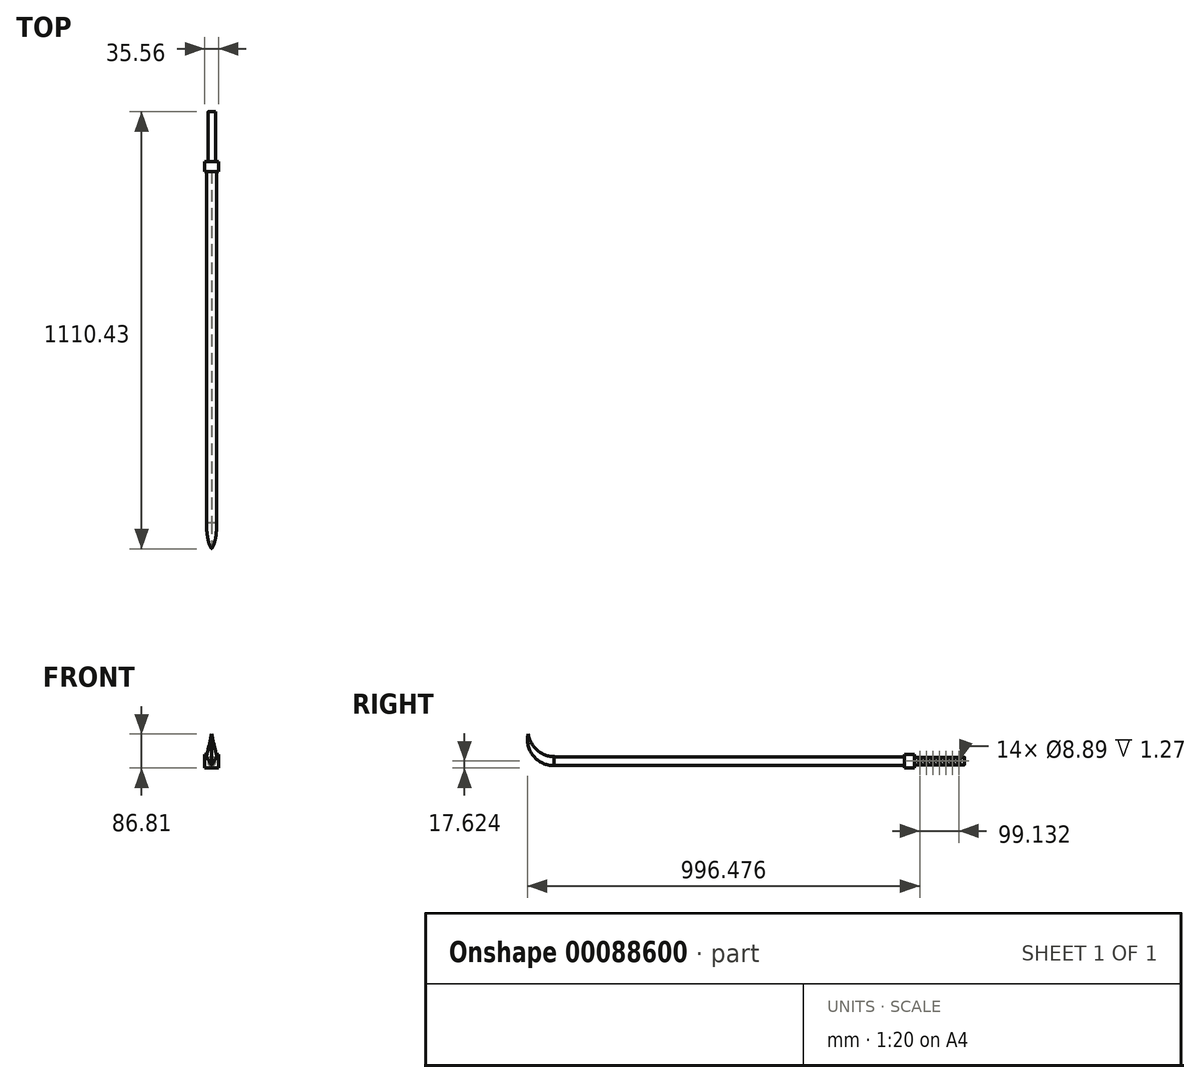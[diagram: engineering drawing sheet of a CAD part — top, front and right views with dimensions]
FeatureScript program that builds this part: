
annotation { "Feature Type Name" : "Feature", "Feature Type Description" : "" }
export const myFeature = defineFeature(function(context is Context, id is Id, definition is map)
    precondition{}
    {
        {
            var Q0;
            Q0=qCreatedBy(makeId("Right.planeOp"),FACE);
            var sketch = newSketch(context, id + "F0", { "sketchPlane" : qUnion([Q0])});
            skArc(sketch, "E0", {"start": v(-281.73, 35.1) * mm, "mid": v(-258.73, -6.34) * mm, "end": v(-214.29, -22.8) * mm});
            skArc(sketch, "E1", {"start": v(-281.73, 35.1) * mm, "mid": v(-268.38, -21.13) * mm, "end": v(-215.9, -45.35) * mm});
            skLineSegment(sketch, "E2", {"start": v(-214.29, -22.8) * mm, "end": v(674.71, -22.8) * mm});
            skLineSegment(sketch, "E3", {"start": v(-215.9, -45.35) * mm, "end": v(674.71, -45.35) * mm});
            skLineSegment(sketch, "E4", {"start": v(674.71, -22.8) * mm, "end": v(674.71, -45.35) * mm});
            skSolve(sketch);
        }
        {
            var Q0;
            Q0 = qSketchRegion(id + "F0", true);
            extrude(context, id + "F1", {"entities" : qUnion([Q0]), "depth" : 25.4 * mm});
        }
        {
            var Q0;
            Q0=makeQuery(id+"F1.opExtrude","SWEPT_FACE",FACE,{"disambiguationData":[OSD([sQuery(id+"F0.wireOp",EDGE,"E4")])]});
            var sketch = newSketch(context, id + "F2", { "sketchPlane" : qUnion([Q0])});
            skLineSegment(sketch, "E5", {"start": v(-25.4, -22.8) * mm, "end": v(-12.7, -45.35) * mm});
            skLineSegment(sketch, "E6", {"start": v(-12.7, -45.35) * mm, "end": v(0, -22.8) * mm});
            skSolve(sketch);
        }
        {
            var Q0;
            {var subQ0=sQuery(id+"F2.wireOp",EDGE,"E5");Q0=makeQuery(id+"F2.imprint","IMPRINT",FACE,{"disambiguationData":[TD([[makeQuery(id+"F2.imprint","IMPRINT",EDGE,{"derivedFrom":subQ0}),-1.0]])]});}
            var Q1;
            {var subQ0=sQuery(id+"F2.wireOp",EDGE,"E6");Q1=makeQuery(id+"F2.imprint","IMPRINT",FACE,{"disambiguationData":[TD([[makeQuery(id+"F2.imprint","IMPRINT",EDGE,{"derivedFrom":subQ0}),-1.0]])]});}
            var Q2;
            Q2=makeQuery(id+"F1.opExtrude","CAP_EDGE",EDGE,{"disambiguationData":[OSD([sQuery(id+"F0.wireOp",EDGE,"E3")])],"isStart":false});
            var Q3;
            Q3=makeQuery(id+"F1.opExtrude","CAP_EDGE",EDGE,{"disambiguationData":[OSD([sQuery(id+"F0.wireOp",EDGE,"E1")])],"isStart":false});
            sweep(context, id + "F3", {"operationType" : NewBodyOperationType.REMOVE, "profiles" : qUnion([Q0, Q1]), "path" : qUnion([Q2, Q3])});
        }
        {
            var Q0;
            Q0=makeQuery(id+"F1.opExtrude","SWEPT_FACE",FACE,{"disambiguationData":[OSD([sQuery(id+"F0.wireOp",EDGE,"E4")])]});
            var sketch = newSketch(context, id + "F4", { "sketchPlane" : qUnion([Q0])});
            skLineSegment(sketch, "E7", {"start": v(-12.7, -45.35) * mm, "end": v(-12.7, -22.8) * mm});
            skLineSegment(sketch, "E8", {"start": v(-12.7, -22.8) * mm, "end": v(-12.7, -16.45) * mm});
            skLineSegment(sketch, "E9", {"start": v(-12.7, -45.35) * mm, "end": v(-12.7, -51.7) * mm});
            skLineSegment(sketch, "E10", {"start": v(-12.7, -16.45) * mm, "end": v(-30.48, -16.45) * mm});
            skLineSegment(sketch, "E11", {"start": v(-12.7, -16.45) * mm, "end": v(5.08, -16.45) * mm});
            skLineSegment(sketch, "E12", {"start": v(-12.7, -51.7) * mm, "end": v(5.08, -51.7) * mm});
            skLineSegment(sketch, "E13", {"start": v(5.08, -51.7) * mm, "end": v(5.08, -16.45) * mm});
            skLineSegment(sketch, "E14", {"start": v(-12.7, -51.7) * mm, "end": v(-30.48, -51.7) * mm});
            skLineSegment(sketch, "E15", {"start": v(-30.48, -51.7) * mm, "end": v(-30.48, -16.45) * mm});
            skLineSegment(sketch, "E16", {"start": v(-19.05, -34.08) * mm, "end": v(-30.48, -34.08) * mm});
            skLineSegment(sketch, "E17", {"start": v(-6.35, -34.08) * mm, "end": v(5.08, -34.08) * mm});
            skSolve(sketch);
        }
        {
            var Q0;
            Q0 = qSketchRegion(id + "F4", true);
            extrude(context, id + "F5", {"entities" : qUnion([Q0]), "depth" : 25.4 * mm});
        }
        {
            var Q0;
            Q0=makeQuery(id+"F5.opExtrude","CAP_FACE",FACE,{"disambiguationData":[OSD([sQuery(id+"F4.wireOp",EDGE,"E10"),sQuery(id+"F4.wireOp",EDGE,"E11"),sQuery(id+"F4.wireOp",EDGE,"E12"),sQuery(id+"F4.wireOp",EDGE,"E13"),sQuery(id+"F4.wireOp",EDGE,"E14"),sQuery(id+"F4.wireOp",EDGE,"E15")])],"isStart":false});
            var sketch = newSketch(context, id + "F6", { "sketchPlane" : qUnion([Q0])});
            skLineSegment(sketch, "E18", {"start": v(-12.7, -34.08) * mm, "end": v(-12.7, -24.55) * mm});
            skLineSegment(sketch, "E19", {"start": v(-12.7, -34.08) * mm, "end": v(-12.7, -43.6) * mm});
            skLineSegment(sketch, "E20", {"start": v(-12.7, -34.08) * mm, "end": v(-3.18, -34.08) * mm});
            skLineSegment(sketch, "E21", {"start": v(-12.7, -34.08) * mm, "end": v(-22.22, -34.08) * mm});
            skLineSegment(sketch, "E22", {"start": v(-22.22, -34.08) * mm, "end": v(-22.22, -24.55) * mm});
            skLineSegment(sketch, "E23", {"start": v(-22.22, -24.55) * mm, "end": v(-3.18, -24.55) * mm});
            skLineSegment(sketch, "E24", {"start": v(-3.18, -24.55) * mm, "end": v(-3.18, -43.6) * mm});
            skLineSegment(sketch, "E25", {"start": v(-3.18, -43.6) * mm, "end": v(-22.22, -43.6) * mm});
            skLineSegment(sketch, "E26", {"start": v(-22.22, -43.6) * mm, "end": v(-22.22, -34.08) * mm});
            skSolve(sketch);
        }
        {
            var Q0;
            Q0 = qSketchRegion(id + "F6", true);
            extrude(context, id + "F7", {"entities" : qUnion([Q0]), "operationType" : NewBodyOperationType.ADD, "depth" : 127 * mm});
        }
        {
            var Q0;
            Q0=makeQuery(id+"F7.opExtrude","SWEPT_EDGE",EDGE,{"disambiguationData":[OSD([sQuery(id+"F6.wireOp",EDGE,"E22"),sQuery(id+"F6.wireOp",EDGE,"E23")])]});
            var Q1;
            Q1=makeQuery(id+"F7.opExtrude","SWEPT_EDGE",EDGE,{"disambiguationData":[OSD([sQuery(id+"F6.wireOp",EDGE,"E23"),sQuery(id+"F6.wireOp",EDGE,"E24")])]});
            var Q2;
            Q2=makeQuery(id+"F7.opExtrude","SWEPT_EDGE",EDGE,{"disambiguationData":[OSD([sQuery(id+"F6.wireOp",EDGE,"E25"),sQuery(id+"F6.wireOp",EDGE,"E26")])]});
            var Q3;
            Q3=makeQuery(id+"F7.opExtrude","SWEPT_EDGE",EDGE,{"disambiguationData":[OSD([sQuery(id+"F6.wireOp",EDGE,"E24"),sQuery(id+"F6.wireOp",EDGE,"E25")])]});
            fillet(context, id + "F8", {"entities" : qUnion([Q0, Q1, Q2, Q3]), "radius" : 5.08 * mm, "tangentPropagation" : true, "allowEdgeOverflow" : false});
        }
        {
            var Q0;
            Q0=makeQuery(id+"F7.opExtrude","SWEPT_FACE",FACE,{"disambiguationData":[OSD([sQuery(id+"F6.wireOp",EDGE,"E24")])]});
            var sketch = newSketch(context, id + "F9", { "sketchPlane" : qUnion([Q0])});
            skLineSegment(sketch, "E27", {"start": v(-812.22, -29.63) * mm, "end": v(-812.22, -38.52) * mm});
            skCircle(sketch, "E28", {"center": v(-812.22, -34.08) * mm, "radius": 4.44 * mm});
            skCircle(sketch, "E29.1.0.0", {"center": v(-795.7, -34.08) * mm, "radius": 4.44 * mm});
            skCircle(sketch, "E29.2.0.0", {"center": v(-779.2, -34.08) * mm, "radius": 4.44 * mm});
            skCircle(sketch, "E29.3.0.0", {"center": v(-762.69, -34.08) * mm, "radius": 4.44 * mm});
            skCircle(sketch, "E29.4.0.0", {"center": v(-746.18, -34.08) * mm, "radius": 4.44 * mm});
            skCircle(sketch, "E29.5.0.0", {"center": v(-729.67, -34.08) * mm, "radius": 4.44 * mm});
            skCircle(sketch, "E29.6.0.0", {"center": v(-713.16, -34.08) * mm, "radius": 4.44 * mm});
            skLineSegment(sketch, "E29.direction1", {"start": v(-812.22, -34.08) * mm, "end": v(-795.7, -34.08) * mm, "construction": true});
            skSolve(sketch);
        }
        {
            var Q0;
            Q0=makeQuery(id+"F7.opExtrude","SWEPT_FACE",FACE,{"disambiguationData":[OSD([sQuery(id+"F6.wireOp",EDGE,"E22"),sQuery(id+"F6.wireOp",EDGE,"E26")])]});
            var sketch = newSketch(context, id + "F10", { "sketchPlane" : qUnion([Q0])});
            skLineSegment(sketch, "E30", {"start": v(812.29, -29.63) * mm, "end": v(812.29, -38.52) * mm});
            skCircle(sketch, "E31", {"center": v(812.29, -34.08) * mm, "radius": 4.44 * mm});
            skCircle(sketch, "E32.1.0.0", {"center": v(795.78, -34.08) * mm, "radius": 4.44 * mm});
            skCircle(sketch, "E32.2.0.0", {"center": v(779.27, -34.08) * mm, "radius": 4.44 * mm});
            skCircle(sketch, "E32.3.0.0", {"center": v(762.76, -34.08) * mm, "radius": 4.44 * mm});
            skCircle(sketch, "E32.4.0.0", {"center": v(746.25, -34.08) * mm, "radius": 4.44 * mm});
            skCircle(sketch, "E32.5.0.0", {"center": v(729.74, -34.08) * mm, "radius": 4.44 * mm});
            skCircle(sketch, "E32.6.0.0", {"center": v(713.23, -34.08) * mm, "radius": 4.44 * mm});
            skLineSegment(sketch, "E32.direction1", {"start": v(812.29, -34.08) * mm, "end": v(795.78, -34.08) * mm, "construction": true});
            skSolve(sketch);
        }
        {
            var Q0;
            {var subQ0=sQuery(id+"F10.wireOp",EDGE,"E32.6.0.0");var subQ1=sQuery(id+"F6.wireOp",EDGE,"E26");var subQ2=sQuery(id+"F6.wireOp",EDGE,"E22");var subQ3=makeQuery(id+"F7.opExtrude","SWEPT_FACE",FACE,{"disambiguationData":[OSD([subQ2,subQ1])]});var subQ4=makeQuery(id+"F10.imprint","INTERSECT",VERTEX,{"derivedFrom":[makeQuery(id+"F8.opFillet","BLEND_EDGE",EDGE,{"blendedFrom":[makeQuery(id+"F7.opExtrude","SWEPT_EDGE",EDGE,{"disambiguationData":[OSD([subQ2,sQuery(id+"F6.wireOp",EDGE,"E23")])]}),subQ3],"blendedInto":[subQ3]}),subQ0]});Q0=makeQuery(id+"F10.imprint","IMPRINT",FACE,{"disambiguationData":[TD([[makeQuery(id+"F10.imprint","IMPRINT",EDGE,{"disambiguationData":[TD([[subQ4,-1.0]])],"derivedFrom":subQ0}),1.0]])]});}
            var Q1;
            {var subQ0=sQuery(id+"F10.wireOp",EDGE,"E32.5.0.0");var subQ1=sQuery(id+"F6.wireOp",EDGE,"E26");var subQ2=sQuery(id+"F6.wireOp",EDGE,"E22");var subQ3=makeQuery(id+"F7.opExtrude","SWEPT_FACE",FACE,{"disambiguationData":[OSD([subQ2,subQ1])]});var subQ4=makeQuery(id+"F10.imprint","INTERSECT",VERTEX,{"derivedFrom":[makeQuery(id+"F8.opFillet","BLEND_EDGE",EDGE,{"blendedFrom":[makeQuery(id+"F7.opExtrude","SWEPT_EDGE",EDGE,{"disambiguationData":[OSD([subQ2,sQuery(id+"F6.wireOp",EDGE,"E23")])]}),subQ3],"blendedInto":[subQ3]}),subQ0]});Q1=makeQuery(id+"F10.imprint","IMPRINT",FACE,{"disambiguationData":[TD([[makeQuery(id+"F10.imprint","IMPRINT",EDGE,{"disambiguationData":[TD([[subQ4,-1.0]])],"derivedFrom":subQ0}),1.0]])]});}
            var Q2;
            {var subQ0=sQuery(id+"F10.wireOp",EDGE,"E32.4.0.0");var subQ1=sQuery(id+"F6.wireOp",EDGE,"E26");var subQ2=sQuery(id+"F6.wireOp",EDGE,"E22");var subQ3=makeQuery(id+"F7.opExtrude","SWEPT_FACE",FACE,{"disambiguationData":[OSD([subQ2,subQ1])]});var subQ4=makeQuery(id+"F10.imprint","INTERSECT",VERTEX,{"derivedFrom":[makeQuery(id+"F8.opFillet","BLEND_EDGE",EDGE,{"blendedFrom":[makeQuery(id+"F7.opExtrude","SWEPT_EDGE",EDGE,{"disambiguationData":[OSD([subQ2,sQuery(id+"F6.wireOp",EDGE,"E23")])]}),subQ3],"blendedInto":[subQ3]}),subQ0]});Q2=makeQuery(id+"F10.imprint","IMPRINT",FACE,{"disambiguationData":[TD([[makeQuery(id+"F10.imprint","IMPRINT",EDGE,{"disambiguationData":[TD([[subQ4,-1.0]])],"derivedFrom":subQ0}),1.0]])]});}
            var Q3;
            {var subQ0=sQuery(id+"F10.wireOp",EDGE,"E32.3.0.0");var subQ1=sQuery(id+"F6.wireOp",EDGE,"E26");var subQ2=sQuery(id+"F6.wireOp",EDGE,"E22");var subQ3=makeQuery(id+"F7.opExtrude","SWEPT_FACE",FACE,{"disambiguationData":[OSD([subQ2,subQ1])]});var subQ4=makeQuery(id+"F10.imprint","INTERSECT",VERTEX,{"derivedFrom":[makeQuery(id+"F8.opFillet","BLEND_EDGE",EDGE,{"blendedFrom":[makeQuery(id+"F7.opExtrude","SWEPT_EDGE",EDGE,{"disambiguationData":[OSD([subQ2,sQuery(id+"F6.wireOp",EDGE,"E23")])]}),subQ3],"blendedInto":[subQ3]}),subQ0]});Q3=makeQuery(id+"F10.imprint","IMPRINT",FACE,{"disambiguationData":[TD([[makeQuery(id+"F10.imprint","IMPRINT",EDGE,{"disambiguationData":[TD([[subQ4,-1.0]])],"derivedFrom":subQ0}),1.0]])]});}
            var Q4;
            {var subQ0=sQuery(id+"F10.wireOp",EDGE,"E32.2.0.0");var subQ1=sQuery(id+"F6.wireOp",EDGE,"E26");var subQ2=sQuery(id+"F6.wireOp",EDGE,"E22");var subQ3=makeQuery(id+"F7.opExtrude","SWEPT_FACE",FACE,{"disambiguationData":[OSD([subQ2,subQ1])]});var subQ4=makeQuery(id+"F10.imprint","INTERSECT",VERTEX,{"derivedFrom":[makeQuery(id+"F8.opFillet","BLEND_EDGE",EDGE,{"blendedFrom":[makeQuery(id+"F7.opExtrude","SWEPT_EDGE",EDGE,{"disambiguationData":[OSD([subQ2,sQuery(id+"F6.wireOp",EDGE,"E23")])]}),subQ3],"blendedInto":[subQ3]}),subQ0]});Q4=makeQuery(id+"F10.imprint","IMPRINT",FACE,{"disambiguationData":[TD([[makeQuery(id+"F10.imprint","IMPRINT",EDGE,{"disambiguationData":[TD([[subQ4,-1.0]])],"derivedFrom":subQ0}),1.0]])]});}
            var Q5;
            {var subQ0=sQuery(id+"F10.wireOp",EDGE,"E32.1.0.0");var subQ1=sQuery(id+"F6.wireOp",EDGE,"E26");var subQ2=sQuery(id+"F6.wireOp",EDGE,"E22");var subQ3=makeQuery(id+"F7.opExtrude","SWEPT_FACE",FACE,{"disambiguationData":[OSD([subQ2,subQ1])]});var subQ4=makeQuery(id+"F10.imprint","INTERSECT",VERTEX,{"derivedFrom":[makeQuery(id+"F8.opFillet","BLEND_EDGE",EDGE,{"blendedFrom":[makeQuery(id+"F7.opExtrude","SWEPT_EDGE",EDGE,{"disambiguationData":[OSD([subQ2,sQuery(id+"F6.wireOp",EDGE,"E23")])]}),subQ3],"blendedInto":[subQ3]}),subQ0]});Q5=makeQuery(id+"F10.imprint","IMPRINT",FACE,{"disambiguationData":[TD([[makeQuery(id+"F10.imprint","IMPRINT",EDGE,{"disambiguationData":[TD([[subQ4,-1.0]])],"derivedFrom":subQ0}),1.0]])]});}
            var Q6;
            {var subQ0=sQuery(id+"F10.wireOp",EDGE,"E30");Q6=makeQuery(id+"F10.imprint","IMPRINT",FACE,{"disambiguationData":[TD([[makeQuery(id+"F10.imprint","IMPRINT",EDGE,{"derivedFrom":subQ0}),1.0]])]});}
            var Q7;
            {var subQ0=sQuery(id+"F10.wireOp",EDGE,"E30");Q7=makeQuery(id+"F10.imprint","IMPRINT",FACE,{"disambiguationData":[TD([[makeQuery(id+"F10.imprint","IMPRINT",EDGE,{"derivedFrom":subQ0}),-1.0]])]});}
            var Q8;
            Q8=sQuery(id+"F10.wireOp",EDGE,"E32.6.0.0");
            var Q9;
            Q9=sQuery(id+"F10.wireOp",EDGE,"E32.5.0.0");
            var Q10;
            Q10=sQuery(id+"F10.wireOp",EDGE,"E32.4.0.0");
            var Q11;
            Q11=sQuery(id+"F10.wireOp",EDGE,"E32.3.0.0");
            var Q12;
            Q12=sQuery(id+"F10.wireOp",EDGE,"E32.2.0.0");
            var Q13;
            Q13=sQuery(id+"F10.wireOp",EDGE,"E32.1.0.0");
            var Q14;
            Q14=sQuery(id+"F10.wireOp",EDGE,"E31");
            extrude(context, id + "F11", {"entities" : qUnion([Q0, Q1, Q2, Q3, Q4, Q5, Q6, Q7]), "operationType" : NewBodyOperationType.REMOVE, "surfaceEntities" : qUnion([Q8, Q9, Q10, Q11, Q12, Q13, Q14]), "oppositeDirection" : true, "depth" : 1.27 * mm});
        }
        {
            var Q0;
            {var subQ0=sQuery(id+"F9.wireOp",EDGE,"E27");Q0=makeQuery(id+"F9.imprint","IMPRINT",FACE,{"disambiguationData":[TD([[makeQuery(id+"F9.imprint","IMPRINT",EDGE,{"derivedFrom":subQ0}),1.0]])]});}
            var Q1;
            {var subQ0=sQuery(id+"F9.wireOp",EDGE,"E27");Q1=makeQuery(id+"F9.imprint","IMPRINT",FACE,{"disambiguationData":[TD([[makeQuery(id+"F9.imprint","IMPRINT",EDGE,{"derivedFrom":subQ0}),-1.0]])]});}
            var Q2;
            {var subQ0=sQuery(id+"F9.wireOp",EDGE,"E29.1.0.0");var subQ1=sQuery(id+"F6.wireOp",EDGE,"E24");var subQ2=makeQuery(id+"F7.opExtrude","SWEPT_FACE",FACE,{"disambiguationData":[OSD([subQ1])]});var subQ3=makeQuery(id+"F9.imprint","INTERSECT",VERTEX,{"derivedFrom":[makeQuery(id+"F8.opFillet","BLEND_EDGE",EDGE,{"blendedFrom":[makeQuery(id+"F7.opExtrude","SWEPT_EDGE",EDGE,{"disambiguationData":[OSD([sQuery(id+"F6.wireOp",EDGE,"E23"),subQ1])]}),subQ2],"blendedInto":[subQ2]}),subQ0]});Q2=makeQuery(id+"F9.imprint","IMPRINT",FACE,{"disambiguationData":[TD([[makeQuery(id+"F9.imprint","IMPRINT",EDGE,{"disambiguationData":[TD([[subQ3,-1.0]])],"derivedFrom":subQ0}),1.0]])]});}
            var Q3;
            {var subQ0=sQuery(id+"F9.wireOp",EDGE,"E29.3.0.0");var subQ1=sQuery(id+"F6.wireOp",EDGE,"E24");var subQ2=makeQuery(id+"F7.opExtrude","SWEPT_FACE",FACE,{"disambiguationData":[OSD([subQ1])]});var subQ3=makeQuery(id+"F9.imprint","INTERSECT",VERTEX,{"derivedFrom":[makeQuery(id+"F8.opFillet","BLEND_EDGE",EDGE,{"blendedFrom":[makeQuery(id+"F7.opExtrude","SWEPT_EDGE",EDGE,{"disambiguationData":[OSD([sQuery(id+"F6.wireOp",EDGE,"E23"),subQ1])]}),subQ2],"blendedInto":[subQ2]}),subQ0]});Q3=makeQuery(id+"F9.imprint","IMPRINT",FACE,{"disambiguationData":[TD([[makeQuery(id+"F9.imprint","IMPRINT",EDGE,{"disambiguationData":[TD([[subQ3,-1.0]])],"derivedFrom":subQ0}),1.0]])]});}
            var Q4;
            {var subQ0=sQuery(id+"F9.wireOp",EDGE,"E29.4.0.0");var subQ1=sQuery(id+"F6.wireOp",EDGE,"E24");var subQ2=makeQuery(id+"F7.opExtrude","SWEPT_FACE",FACE,{"disambiguationData":[OSD([subQ1])]});var subQ3=makeQuery(id+"F9.imprint","INTERSECT",VERTEX,{"derivedFrom":[makeQuery(id+"F8.opFillet","BLEND_EDGE",EDGE,{"blendedFrom":[makeQuery(id+"F7.opExtrude","SWEPT_EDGE",EDGE,{"disambiguationData":[OSD([sQuery(id+"F6.wireOp",EDGE,"E23"),subQ1])]}),subQ2],"blendedInto":[subQ2]}),subQ0]});Q4=makeQuery(id+"F9.imprint","IMPRINT",FACE,{"disambiguationData":[TD([[makeQuery(id+"F9.imprint","IMPRINT",EDGE,{"disambiguationData":[TD([[subQ3,-1.0]])],"derivedFrom":subQ0}),1.0]])]});}
            var Q5;
            {var subQ0=sQuery(id+"F9.wireOp",EDGE,"E29.5.0.0");var subQ1=sQuery(id+"F6.wireOp",EDGE,"E24");var subQ2=makeQuery(id+"F7.opExtrude","SWEPT_FACE",FACE,{"disambiguationData":[OSD([subQ1])]});var subQ3=makeQuery(id+"F9.imprint","INTERSECT",VERTEX,{"derivedFrom":[makeQuery(id+"F8.opFillet","BLEND_EDGE",EDGE,{"blendedFrom":[makeQuery(id+"F7.opExtrude","SWEPT_EDGE",EDGE,{"disambiguationData":[OSD([sQuery(id+"F6.wireOp",EDGE,"E23"),subQ1])]}),subQ2],"blendedInto":[subQ2]}),subQ0]});Q5=makeQuery(id+"F9.imprint","IMPRINT",FACE,{"disambiguationData":[TD([[makeQuery(id+"F9.imprint","IMPRINT",EDGE,{"disambiguationData":[TD([[subQ3,-1.0]])],"derivedFrom":subQ0}),1.0]])]});}
            var Q6;
            {var subQ0=sQuery(id+"F9.wireOp",EDGE,"E29.2.0.0");var subQ1=sQuery(id+"F6.wireOp",EDGE,"E24");var subQ2=makeQuery(id+"F7.opExtrude","SWEPT_FACE",FACE,{"disambiguationData":[OSD([subQ1])]});var subQ3=makeQuery(id+"F9.imprint","INTERSECT",VERTEX,{"derivedFrom":[makeQuery(id+"F8.opFillet","BLEND_EDGE",EDGE,{"blendedFrom":[makeQuery(id+"F7.opExtrude","SWEPT_EDGE",EDGE,{"disambiguationData":[OSD([sQuery(id+"F6.wireOp",EDGE,"E23"),subQ1])]}),subQ2],"blendedInto":[subQ2]}),subQ0]});Q6=makeQuery(id+"F9.imprint","IMPRINT",FACE,{"disambiguationData":[TD([[makeQuery(id+"F9.imprint","IMPRINT",EDGE,{"disambiguationData":[TD([[subQ3,-1.0]])],"derivedFrom":subQ0}),1.0]])]});}
            var Q7;
            {var subQ0=sQuery(id+"F9.wireOp",EDGE,"E29.6.0.0");var subQ1=sQuery(id+"F6.wireOp",EDGE,"E24");var subQ2=makeQuery(id+"F7.opExtrude","SWEPT_FACE",FACE,{"disambiguationData":[OSD([subQ1])]});var subQ3=makeQuery(id+"F9.imprint","INTERSECT",VERTEX,{"derivedFrom":[makeQuery(id+"F8.opFillet","BLEND_EDGE",EDGE,{"blendedFrom":[makeQuery(id+"F7.opExtrude","SWEPT_EDGE",EDGE,{"disambiguationData":[OSD([sQuery(id+"F6.wireOp",EDGE,"E23"),subQ1])]}),subQ2],"blendedInto":[subQ2]}),subQ0]});Q7=makeQuery(id+"F9.imprint","IMPRINT",FACE,{"disambiguationData":[TD([[makeQuery(id+"F9.imprint","IMPRINT",EDGE,{"disambiguationData":[TD([[subQ3,-1.0]])],"derivedFrom":subQ0}),1.0]])]});}
            extrude(context, id + "F12", {"entities" : qUnion([Q0, Q1, Q2, Q3, Q4, Q5, Q6, Q7]), "operationType" : NewBodyOperationType.REMOVE, "oppositeDirection" : true, "depth" : 1.27 * mm});
        }
        {
            var Q0;
            Q0=makeQuery(id+"F11.boolean.opBoolean","COPY",FACE,{"derivedFrom":makeQuery(id+"F11.opExtrude","CAP_FACE",FACE,{"disambiguationData":[OSD([sQuery(id+"F10.wireOp",EDGE,"E31")])],"isStart":false})});
            var Q1;
            Q1=makeQuery(id+"F11.boolean.opBoolean","COPY",FACE,{"derivedFrom":makeQuery(id+"F11.opExtrude","CAP_FACE",FACE,{"disambiguationData":[OSD([sQuery(id+"F10.wireOp",EDGE,"E32.1.0.0")])],"isStart":false})});
            var Q2;
            Q2=makeQuery(id+"F11.boolean.opBoolean","COPY",FACE,{"derivedFrom":makeQuery(id+"F11.opExtrude","CAP_FACE",FACE,{"disambiguationData":[OSD([sQuery(id+"F10.wireOp",EDGE,"E32.2.0.0")])],"isStart":false})});
            var Q3;
            Q3=makeQuery(id+"F11.boolean.opBoolean","COPY",FACE,{"derivedFrom":makeQuery(id+"F11.opExtrude","CAP_FACE",FACE,{"disambiguationData":[OSD([sQuery(id+"F10.wireOp",EDGE,"E32.3.0.0")])],"isStart":false})});
            var Q4;
            Q4=makeQuery(id+"F11.boolean.opBoolean","COPY",FACE,{"derivedFrom":makeQuery(id+"F11.opExtrude","CAP_FACE",FACE,{"disambiguationData":[OSD([sQuery(id+"F10.wireOp",EDGE,"E32.4.0.0")])],"isStart":false})});
            var Q5;
            Q5=makeQuery(id+"F11.boolean.opBoolean","COPY",FACE,{"derivedFrom":makeQuery(id+"F11.opExtrude","CAP_FACE",FACE,{"disambiguationData":[OSD([sQuery(id+"F10.wireOp",EDGE,"E32.5.0.0")])],"isStart":false})});
            var Q6;
            Q6=makeQuery(id+"F11.boolean.opBoolean","COPY",FACE,{"derivedFrom":makeQuery(id+"F11.opExtrude","CAP_FACE",FACE,{"disambiguationData":[OSD([sQuery(id+"F10.wireOp",EDGE,"E32.6.0.0")])],"isStart":false})});
            extrude(context, id + "F13", {"entities" : qUnion([Q0, Q1, Q2, Q3, Q4, Q5, Q6]), "depth" : 0.64 * mm});
        }
        {
            var Q0;
            Q0=makeQuery(id+"F12.boolean.opBoolean","COPY",FACE,{"derivedFrom":makeQuery(id+"F12.opExtrude","CAP_FACE",FACE,{"disambiguationData":[OSD([sQuery(id+"F9.wireOp",EDGE,"E29.6.0.0")])],"isStart":false})});
            var Q1;
            Q1=makeQuery(id+"F12.boolean.opBoolean","COPY",FACE,{"derivedFrom":makeQuery(id+"F12.opExtrude","CAP_FACE",FACE,{"disambiguationData":[OSD([sQuery(id+"F9.wireOp",EDGE,"E29.5.0.0")])],"isStart":false})});
            var Q2;
            Q2=makeQuery(id+"F12.boolean.opBoolean","COPY",FACE,{"derivedFrom":makeQuery(id+"F12.opExtrude","CAP_FACE",FACE,{"disambiguationData":[OSD([sQuery(id+"F9.wireOp",EDGE,"E29.4.0.0")])],"isStart":false})});
            var Q3;
            Q3=makeQuery(id+"F12.boolean.opBoolean","COPY",FACE,{"derivedFrom":makeQuery(id+"F12.opExtrude","CAP_FACE",FACE,{"disambiguationData":[OSD([sQuery(id+"F9.wireOp",EDGE,"E29.3.0.0")])],"isStart":false})});
            var Q4;
            Q4=makeQuery(id+"F12.boolean.opBoolean","COPY",FACE,{"derivedFrom":makeQuery(id+"F12.opExtrude","CAP_FACE",FACE,{"disambiguationData":[OSD([sQuery(id+"F9.wireOp",EDGE,"E29.2.0.0")])],"isStart":false})});
            var Q5;
            Q5=makeQuery(id+"F12.boolean.opBoolean","COPY",FACE,{"derivedFrom":makeQuery(id+"F12.opExtrude","CAP_FACE",FACE,{"disambiguationData":[OSD([sQuery(id+"F9.wireOp",EDGE,"E29.1.0.0")])],"isStart":false})});
            var Q6;
            Q6=makeQuery(id+"F12.boolean.opBoolean","COPY",FACE,{"derivedFrom":makeQuery(id+"F12.opExtrude","CAP_FACE",FACE,{"disambiguationData":[OSD([sQuery(id+"F9.wireOp",EDGE,"E28")])],"isStart":false})});
            extrude(context, id + "F14", {"entities" : qUnion([Q0, Q1, Q2, Q3, Q4, Q5, Q6]), "depth" : 0.64 * mm});
        }
    });
